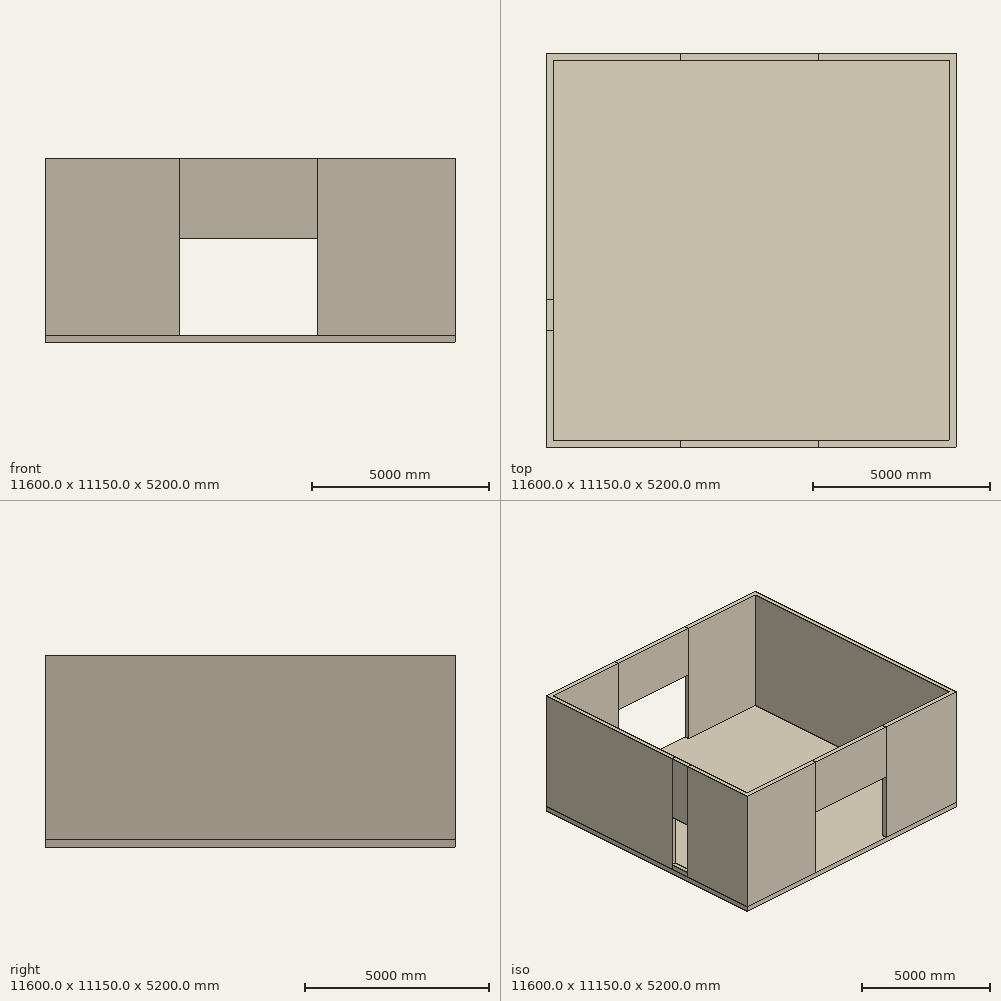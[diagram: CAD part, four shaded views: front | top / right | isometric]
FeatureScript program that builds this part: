
annotation { "Feature Type Name" : "Feature", "Feature Type Description" : "" }
export const myFeature = defineFeature(function(context is Context, id is Id, definition is map)
    precondition{}
    {
        {
            var Q0;
            Q0=qCreatedBy(makeId("Top.planeOp"),FACE);
            var sketch = newSketch(context, id + "F0", { "sketchPlane" : qUnion([Q0])});
            skLineSegment(sketch, "E0.bottom", {"start": v(5600, -5375) * mm, "end": v(1900, -5375) * mm});
            skLineSegment(sketch, "E0.top", {"start": v(5600, 5375) * mm, "end": v(1900, 5375) * mm});
            skLineSegment(sketch, "E0.left", {"start": v(5600, -5375) * mm, "end": v(5600, 5375) * mm});
            skLineSegment(sketch, "E0.right", {"start": v(-5600, -5375) * mm, "end": v(-5600, -2275) * mm});
            skPoint(sketch, "E0.middle", {"position": v(0, 0) * mm});
            skLineSegment(sketch, "E1.0", {"start": v(5800, -5575) * mm, "end": v(5800, 5575) * mm});
            skLineSegment(sketch, "E1.1", {"start": v(5800, -5575) * mm, "end": v(1900, -5575) * mm});
            skLineSegment(sketch, "E1.2", {"start": v(-5800, -5575) * mm, "end": v(-5800, -2275) * mm});
            skLineSegment(sketch, "E1.3", {"start": v(5800, 5575) * mm, "end": v(1900, 5575) * mm});
            skLineSegment(sketch, "E2", {"start": v(-5600, -2275) * mm, "end": v(-5800, -2275) * mm});
            skLineSegment(sketch, "E3", {"start": v(-5600, -1395) * mm, "end": v(-5800, -1395) * mm});
            skLineSegment(sketch, "E4", {"start": v(-2000, -5375) * mm, "end": v(-2000, -5575) * mm});
            skLineSegment(sketch, "E5", {"start": v(1900, -5575) * mm, "end": v(1900, -5375) * mm});
            skLineSegment(sketch, "E6", {"start": v(-2000, 5575) * mm, "end": v(-2000, 5375) * mm});
            skLineSegment(sketch, "E7", {"start": v(1900, 5575) * mm, "end": v(1900, 5375) * mm});
            skLineSegment(sketch, "E8.trimOffspring", {"start": v(-2000, 5575) * mm, "end": v(-5800, 5575) * mm});
            skLineSegment(sketch, "E9.trimOffspring", {"start": v(-2000, 5375) * mm, "end": v(-5600, 5375) * mm});
            skLineSegment(sketch, "E10.trimOffspring", {"start": v(-2000, -5375) * mm, "end": v(-5600, -5375) * mm});
            skLineSegment(sketch, "E11.trimOffspring", {"start": v(-2000, -5575) * mm, "end": v(-5800, -5575) * mm});
            skLineSegment(sketch, "E12.trimOffspring", {"start": v(-5800, -1395) * mm, "end": v(-5800, 5575) * mm});
            skLineSegment(sketch, "E13.trimOffspring", {"start": v(-5600, -1395) * mm, "end": v(-5600, 5375) * mm});
            skSolve(sketch);
        }
        {
            var Q0;
            Q0=makeQuery(id+"F0.imprint","IMPRINT",FACE,{"disambiguationData":[TD([[makeQuery(id+"F0.imprint","IMPRINT",EDGE,{"derivedFrom":sQuery(id+"F0.wireOp",EDGE,"E3")}),-1.0]])]});
            var Q1;
            Q1=makeQuery(id+"F0.imprint","IMPRINT",FACE,{"disambiguationData":[TD([[makeQuery(id+"F0.imprint","IMPRINT",EDGE,{"derivedFrom":sQuery(id+"F0.wireOp",EDGE,"E0.right")}),1.0]])]});
            var Q2;
            Q2=makeQuery(id+"F0.imprint","IMPRINT",FACE,{"disambiguationData":[TD([[makeQuery(id+"F0.imprint","IMPRINT",EDGE,{"derivedFrom":sQuery(id+"F0.wireOp",EDGE,"E0.bottom")}),1.0]])]});
            extrude(context, id + "F1", {"entities" : qUnion([Q0, Q1, Q2]), "depth" : 5000 * mm, "offsetDistance" : 25 * mm});
        }
        {
            var Q0;
            Q0=qCreatedBy(makeId("Top.planeOp"),FACE);
            var sketch = newSketch(context, id + "F2", { "sketchPlane" : qUnion([Q0])});
            skLineSegment(sketch, "E14.bottom", {"start": v(-5800, -1395) * mm, "end": v(-5600, -1395) * mm});
            skLineSegment(sketch, "E14.top", {"start": v(-5800, -2275) * mm, "end": v(-5600, -2275) * mm});
            skLineSegment(sketch, "E14.left", {"start": v(-5800, -1395) * mm, "end": v(-5800, -2275) * mm});
            skLineSegment(sketch, "E14.right", {"start": v(-5600, -1395) * mm, "end": v(-5600, -2275) * mm});
            skSolve(sketch);
        }
        {
            var Q0;
            Q0=makeQuery(id+"F2.imprint","IMPRINT",FACE,{"disambiguationData":[TD([[makeQuery(id+"F2.imprint","IMPRINT",EDGE,{"derivedFrom":sQuery(id+"F2.wireOp",EDGE,"E14.bottom")}),-1.0]])]});
            extrude(context, id + "F3", {"entities" : qUnion([Q0]), "depth" : 200 * mm, "offsetDistance" : 25 * mm});
        }
        {
            var Q0;
            Q0=makeQuery(id+"F1.opExtrude","CAP_FACE",FACE,{"disambiguationData":[OSD([sQuery(id+"F0.wireOp",EDGE,"E0.bottom"),sQuery(id+"F0.wireOp",EDGE,"E0.top"),sQuery(id+"F0.wireOp",EDGE,"E0.left"),sQuery(id+"F0.wireOp",EDGE,"E1.0"),sQuery(id+"F0.wireOp",EDGE,"E1.1"),sQuery(id+"F0.wireOp",EDGE,"E1.3"),sQuery(id+"F0.wireOp",EDGE,"E5"),sQuery(id+"F0.wireOp",EDGE,"E7")])],"isStart":false});
            var sketch = newSketch(context, id + "F4", { "sketchPlane" : qUnion([Q0])});
            skLineSegment(sketch, "E15.bottom", {"start": v(1900, 5575) * mm, "end": v(-2000, 5575) * mm});
            skLineSegment(sketch, "E15.top", {"start": v(1900, 5375) * mm, "end": v(-2000, 5375) * mm});
            skLineSegment(sketch, "E15.left", {"start": v(1900, 5575) * mm, "end": v(1900, 5375) * mm});
            skLineSegment(sketch, "E15.right", {"start": v(-2000, 5575) * mm, "end": v(-2000, 5375) * mm});
            skLineSegment(sketch, "E16.bottom", {"start": v(1900, -5375) * mm, "end": v(-2000, -5375) * mm});
            skLineSegment(sketch, "E16.top", {"start": v(1900, -5575) * mm, "end": v(-2000, -5575) * mm});
            skLineSegment(sketch, "E16.left", {"start": v(1900, -5375) * mm, "end": v(1900, -5575) * mm});
            skLineSegment(sketch, "E16.right", {"start": v(-2000, -5375) * mm, "end": v(-2000, -5575) * mm});
            skLineSegment(sketch, "E17.bottom", {"start": v(-5600, -1395) * mm, "end": v(-5800, -1395) * mm});
            skLineSegment(sketch, "E17.top", {"start": v(-5600, -2275) * mm, "end": v(-5800, -2275) * mm});
            skLineSegment(sketch, "E17.left", {"start": v(-5600, -1395) * mm, "end": v(-5600, -2275) * mm});
            skLineSegment(sketch, "E17.right", {"start": v(-5800, -1395) * mm, "end": v(-5800, -2275) * mm});
            skSolve(sketch);
        }
        {
            var Q0;
            Q0=makeQuery(id+"F4.imprint","IMPRINT",FACE,{"disambiguationData":[TD([[makeQuery(id+"F4.imprint","IMPRINT",EDGE,{"derivedFrom":sQuery(id+"F4.wireOp",EDGE,"E16.bottom")}),1.0]])]});
            extrude(context, id + "F5", {"entities" : qUnion([Q0]), "oppositeDirection" : true, "depth" : 2250 * mm, "offsetDistance" : 25 * mm});
        }
        {
            var Q0;
            Q0=makeQuery(id+"F4.imprint","IMPRINT",FACE,{"disambiguationData":[TD([[makeQuery(id+"F4.imprint","IMPRINT",EDGE,{"derivedFrom":sQuery(id+"F4.wireOp",EDGE,"E15.bottom")}),1.0]])]});
            extrude(context, id + "F6", {"entities" : qUnion([Q0]), "oppositeDirection" : true, "depth" : 2100 * mm, "offsetDistance" : 25 * mm});
        }
        {
            var Q0;
            Q0=makeQuery(id+"F4.imprint","IMPRINT",FACE,{"disambiguationData":[TD([[makeQuery(id+"F4.imprint","IMPRINT",EDGE,{"derivedFrom":sQuery(id+"F4.wireOp",EDGE,"E17.bottom")}),1.0]])]});
            extrude(context, id + "F7", {"entities" : qUnion([Q0]), "oppositeDirection" : true, "depth" : 2650 * mm, "offsetDistance" : 25 * mm});
        }
        {
            var Q0;
            Q0=qCreatedBy(makeId("Top.planeOp"),FACE);
            var sketch = newSketch(context, id + "F8", { "sketchPlane" : qUnion([Q0])});
            skLineSegment(sketch, "E18.bottom", {"start": v(-5800, -5575) * mm, "end": v(5800, -5575) * mm});
            skLineSegment(sketch, "E18.top", {"start": v(-5800, 5575) * mm, "end": v(5800, 5575) * mm});
            skLineSegment(sketch, "E18.left", {"start": v(-5800, -5575) * mm, "end": v(-5800, 5575) * mm});
            skLineSegment(sketch, "E18.right", {"start": v(5800, -5575) * mm, "end": v(5800, 5575) * mm});
            skSolve(sketch);
        }
        {
            var Q0;
            Q0=makeQuery(id+"F8.imprint","IMPRINT",FACE,{"disambiguationData":[TD([[makeQuery(id+"F8.imprint","IMPRINT",EDGE,{"derivedFrom":sQuery(id+"F8.wireOp",EDGE,"E18.bottom")}),1.0]])]});
            extrude(context, id + "F9", {"entities" : qUnion([Q0]), "oppositeDirection" : true, "depth" : 200 * mm, "offsetDistance" : 25 * mm});
        }
    });
